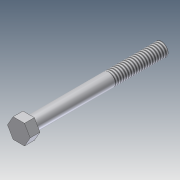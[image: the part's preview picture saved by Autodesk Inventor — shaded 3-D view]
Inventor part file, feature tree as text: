
AUTODESK INVENTOR PART (.ipt)
format: ipt  version: 2012 (Build 160160000, 160)  size: 81,920 bytes
history: native  units: in
note: dims shown in document units (in); Inventor stores cm internally (conversion verified against a paired STEP export)
features: extrude x2, sketch x1, thread x1
ambient origin geometry x8: Origin, YZ Plane, XZ Plane, XY Plane, X Axis, Y Axis, Z Axis, Center Point
bodies: Solid1 (feature_tree)
feature tree (4):
  sketch  "Sketch1"  dims[d10=0.37in d11=2.5in d12=0.0in d13=0.185in d14=0.0in d15=1.0in d16=0.0in]
  extrude  "Extrusion1"  Depth=2.5in TaperAngle=0.0deg
  extrude  "Extrusion2"  Depth=0.185in TaperAngle=0.0deg
  thread  "Thread1"  [1 undecoded]
note: 1 required parameter value undecoded (feature->parameter linkage not recoverable at this tier; creation-order binding heuristic only, values carry confidence <= 0.55)
